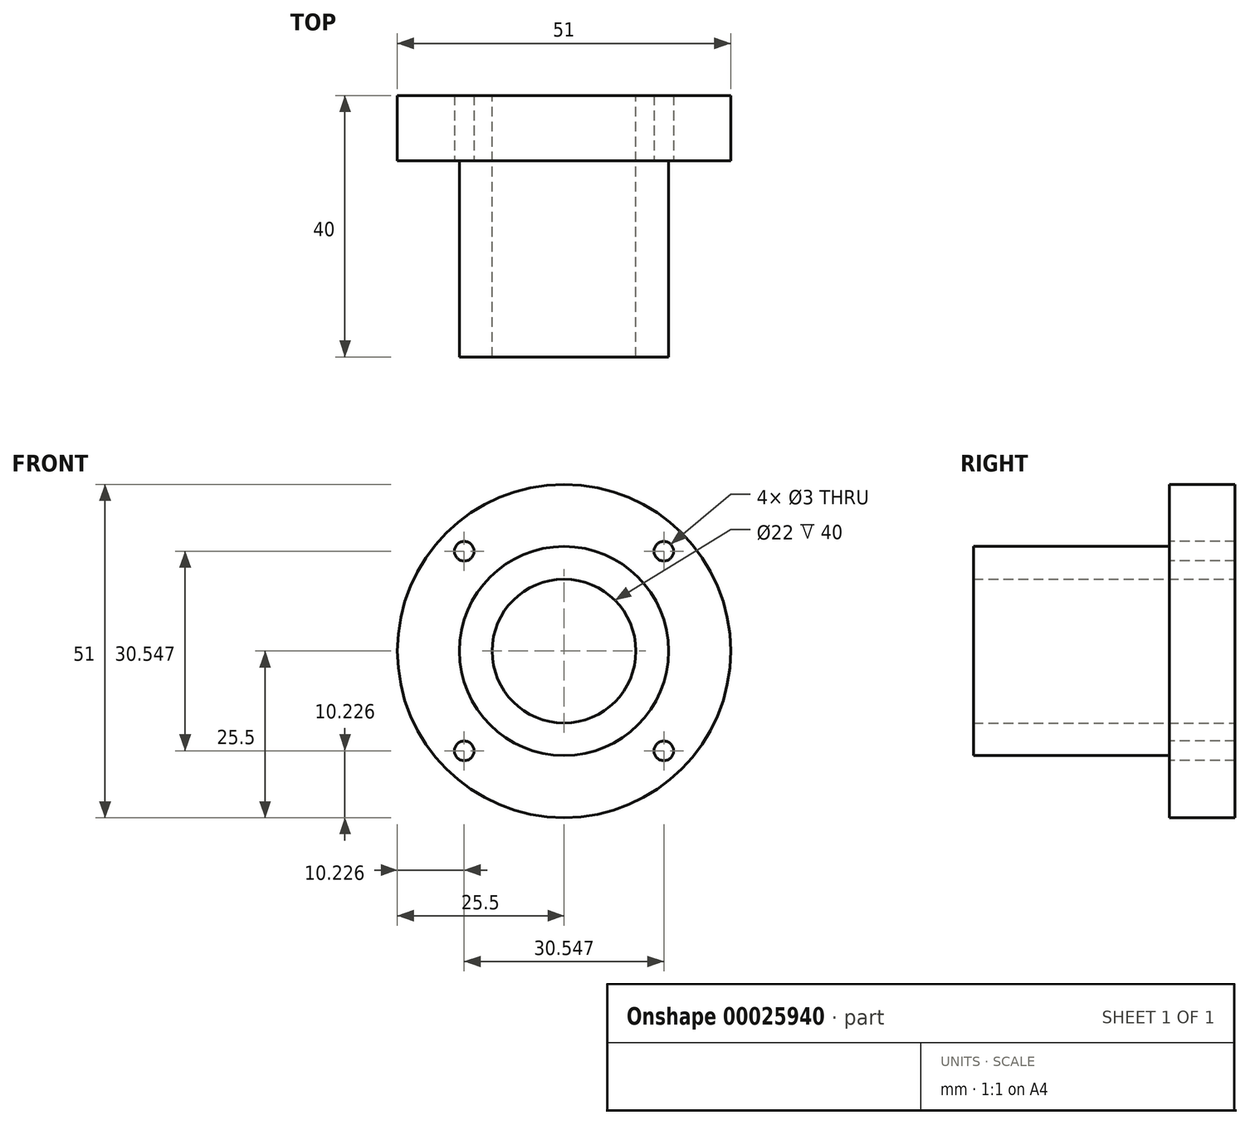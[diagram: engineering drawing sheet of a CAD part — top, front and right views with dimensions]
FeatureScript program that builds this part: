
annotation { "Feature Type Name" : "Feature", "Feature Type Description" : "" }
export const myFeature = defineFeature(function(context is Context, id is Id, definition is map)
    precondition{}
    {
        {
            var Q0;
            Q0=qCreatedBy(makeId("Front.planeOp"),FACE);
            var sketch = newSketch(context, id + "F0", { "sketchPlane" : qUnion([Q0])});
            skCircle(sketch, "E0", {"center": v(0, 0) * mm, "radius": 25.5 * mm});
            skSolve(sketch);
        }
        {
            var Q0;
            Q0=makeQuery(id+"F0.imprint","IMPRINT",FACE,{"disambiguationData":[TD([[makeQuery(id+"F0.imprint","IMPRINT",EDGE,{"derivedFrom":sQuery(id+"F0.wireOp",EDGE,"E0")}),1.0]])]});
            extrude(context, id + "F1", {"entities" : qUnion([Q0]), "depth" : 40 * mm});
        }
        {
            var Q0;
            Q0=makeQuery(id+"F1.opExtrude","CAP_FACE",FACE,{"disambiguationData":[OSD([sQuery(id+"F0.wireOp",EDGE,"E0")])],"isStart":true});
            var sketch = newSketch(context, id + "F2", { "sketchPlane" : qUnion([Q0])});
            skCircle(sketch, "E1", {"center": v(0, 0) * mm, "radius": 11 * mm});
            skSolve(sketch);
        }
        {
            var Q0;
            Q0=makeQuery(id+"F2.imprint","IMPRINT",FACE,{"disambiguationData":[TD([[makeQuery(id+"F2.imprint","IMPRINT",EDGE,{"derivedFrom":sQuery(id+"F2.wireOp",EDGE,"E1")}),1.0]])]});
            extrude(context, id + "F3", {"entities" : qUnion([Q0]), "operationType" : NewBodyOperationType.REMOVE, "endBound" : BoundingType.UP_TO_NEXT, "oppositeDirection" : true, "depth" : 25 * mm});
        }
        {
            var Q0;
            Q0=makeQuery(id+"F1.opExtrude","CAP_FACE",FACE,{"disambiguationData":[OSD([sQuery(id+"F0.wireOp",EDGE,"E0")])],"isStart":false});
            var sketch = newSketch(context, id + "F4", { "sketchPlane" : qUnion([Q0])});
            skCircle(sketch, "E2", {"center": v(0, 0) * mm, "radius": 16 * mm});
            skCircle(sketch, "E3.0", {"center": v(0, 0) * mm, "radius": 25.5 * mm});
            skSolve(sketch);
        }
        {
            var Q0;
            Q0=makeQuery(id+"F4.imprint","IMPRINT",FACE,{"disambiguationData":[TD([[makeQuery(id+"F4.imprint","IMPRINT",EDGE,{"derivedFrom":sQuery(id+"F4.wireOp",EDGE,"E2")}),-1.0]])]});
            extrude(context, id + "F5", {"entities" : qUnion([Q0]), "operationType" : NewBodyOperationType.REMOVE, "oppositeDirection" : true, "depth" : 30 * mm});
        }
        {
            var Q0;
            Q0=makeQuery(id+"F1.opExtrude","CAP_FACE",FACE,{"disambiguationData":[OSD([sQuery(id+"F0.wireOp",EDGE,"E0")])],"isStart":true});
            var sketch = newSketch(context, id + "F6", { "sketchPlane" : qUnion([Q0])});
            skPoint(sketch, "E4", {"position": v(-15.27, -15.27) * mm});
            skLineSegment(sketch, "E5", {"start": v(0, 0) * mm, "end": v(-15.27, -15.27) * mm, "construction": true});
            skLineSegment(sketch, "E6", {"start": v(0, 0) * mm, "end": v(0, -18.4) * mm, "construction": true});
            skPoint(sketch, "E7.1.0", {"position": v(15.27, -15.27) * mm});
            skPoint(sketch, "E7.2.0", {"position": v(15.27, 15.27) * mm});
            skPoint(sketch, "E7.3.0", {"position": v(-15.27, 15.27) * mm});
            skPoint(sketch, "E7.center", {"position": v(0, 0) * mm});
            skSolve(sketch);
        }
        {
            var Q0;
            Q0=sQuery(id+"F6.wireOp",VERTEX,"E7.3.0");
            var Q1;
            Q1=sQuery(id+"F6.wireOp",VERTEX,"E7.2.0");
            var Q2;
            Q2=sQuery(id+"F6.wireOp",VERTEX,"E7.1.0");
            var Q3;
            Q3=sQuery(id+"F6.wireOp",VERTEX,"E4");
            var Q4;
            Q4=makeQuery(id+"F1.opExtrude","SWEPT_BODY",BODY,{"disambiguationData":[OSD([sQuery(id+"F0.wireOp",EDGE,"E0")])]});
            hole(context, id + "F7", {"style" : HoleStyle.SIMPLE, "holeDiameter" : 3 * mm, "endStyle" : HoleEndStyle.THROUGH, "locations" : qUnion([Q0, Q1, Q2, Q3]), "scope" : qUnion([Q4])});
        }
    });
